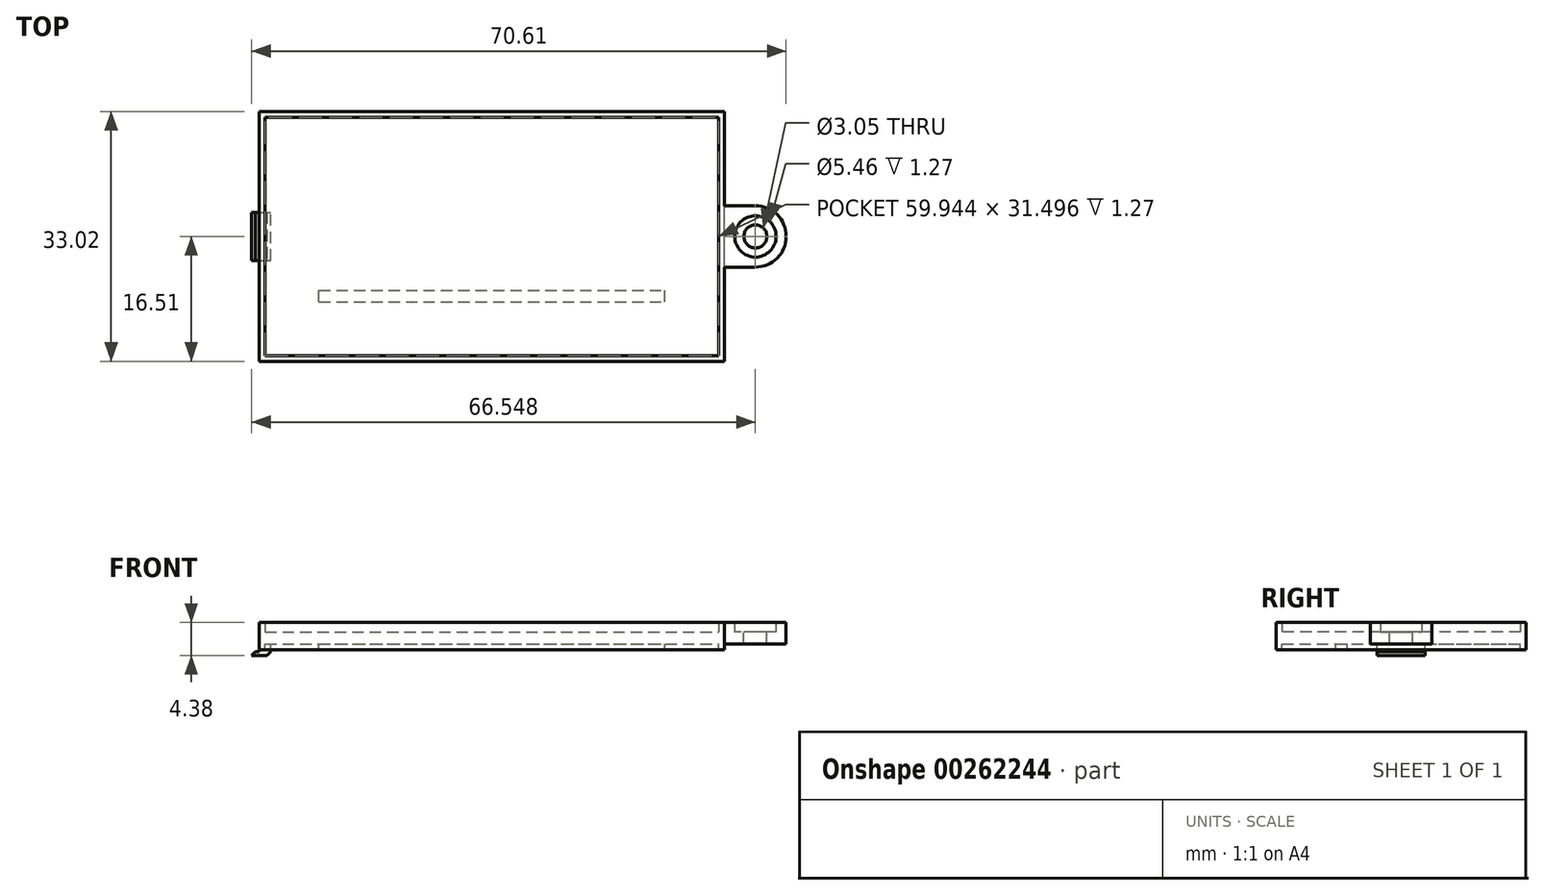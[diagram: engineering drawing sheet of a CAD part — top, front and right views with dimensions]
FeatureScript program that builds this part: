
annotation { "Feature Type Name" : "Feature", "Feature Type Description" : "" }
export const myFeature = defineFeature(function(context is Context, id is Id, definition is map)
    precondition{}
    {
        {
            var Q0;
            Q0=qCreatedBy(makeId("Top.planeOp"),FACE);
            var sketch = newSketch(context, id + "F0", { "sketchPlane" : qUnion([Q0])});
            skLineSegment(sketch, "E0.bottom", {"start": v(30.73, -16.51) * mm, "end": v(-30.73, -16.51) * mm});
            skLineSegment(sketch, "E0.top", {"start": v(30.73, 16.51) * mm, "end": v(-30.73, 16.51) * mm});
            skLineSegment(sketch, "E0.left", {"start": v(30.73, -16.5) * mm, "end": v(30.73, 16.51) * mm});
            skLineSegment(sketch, "E0.right", {"start": v(-30.73, -16.51) * mm, "end": v(-30.73, 16.51) * mm});
            skPoint(sketch, "E0.middle", {"position": v(0, 0) * mm});
            skLineSegment(sketch, "E1", {"start": v(-53.62, 0) * mm, "end": v(52.35, 0) * mm, "construction": true});
            skPoint(sketch, "E1.startSnap0", {"position": v(-30.73, 0) * mm});
            skPoint(sketch, "E1.endSnap0", {"position": v(-30.73, 0) * mm});
            skLineSegment(sketch, "E2", {"start": v(30.73, 4.06) * mm, "end": v(34.8, 4.06) * mm});
            skLineSegment(sketch, "E3", {"start": v(38.86, 0) * mm, "end": v(38.86, 0) * mm});
            skLineSegment(sketch, "E4", {"start": v(34.8, -4.06) * mm, "end": v(30.73, -4.06) * mm});
            skPoint(sketch, "E5.visualSharp", {"position": v(38.86, 4.06) * mm});
            skArc(sketch, "E5.filletArc", {"start": v(38.86, 0) * mm, "mid": v(37.67, 2.87) * mm, "end": v(34.8, 4.06) * mm});
            skPoint(sketch, "E6.visualSharp", {"position": v(38.86, -4.06) * mm});
            skArc(sketch, "E6.filletArc", {"start": v(34.8, -4.06) * mm, "mid": v(37.67, -2.87) * mm, "end": v(38.86, 0) * mm});
            skSolve(sketch);
        }
        {
            var Q0;
            Q0 = qSketchRegion(id + "F0", true);
            extrude(context, id + "F1", {"entities" : qUnion([Q0]), "depth" : 1.59 * mm});
        }
        {
            var Q0;
            Q0=makeQuery(id+"F1.opExtrude","CAP_FACE",FACE,{"disambiguationData":[OSD([sQuery(id+"F0.wireOp",EDGE,"E0.bottom"),sQuery(id+"F0.wireOp",EDGE,"E0.top"),sQuery(id+"F0.wireOp",EDGE,"E0.left"),sQuery(id+"F0.wireOp",EDGE,"E0.right"),sQuery(id+"F0.wireOp",EDGE,"E2"),sQuery(id+"F0.wireOp",EDGE,"E4"),sQuery(id+"F0.wireOp",EDGE,"E5.filletArc"),sQuery(id+"F0.wireOp",EDGE,"E6.filletArc")])],"isStart":false});
            var sketch = newSketch(context, id + "F2", { "sketchPlane" : qUnion([Q0])});
            skCircle(sketch, "E7", {"center": v(34.8, 0) * mm, "radius": 1.52 * mm});
            skSolve(sketch);
        }
        {
            var Q0;
            Q0=makeQuery(id+"F2.imprint","IMPRINT",FACE,{"disambiguationData":[TD([[makeQuery(id+"F2.imprint","IMPRINT",EDGE,{"derivedFrom":sQuery(id+"F2.wireOp",EDGE,"E7")}),1.0]])]});
            extrude(context, id + "F3", {"entities" : qUnion([Q0]), "operationType" : NewBodyOperationType.REMOVE, "endBound" : BoundingType.THROUGH_ALL, "oppositeDirection" : true, "depth" : 25.4 * mm});
        }
        {
            var Q0;
            Q0=makeQuery(id+"F1.opExtrude","CAP_FACE",FACE,{"disambiguationData":[OSD([sQuery(id+"F0.wireOp",EDGE,"E0.bottom"),sQuery(id+"F0.wireOp",EDGE,"E0.top"),sQuery(id+"F0.wireOp",EDGE,"E0.left"),sQuery(id+"F0.wireOp",EDGE,"E0.right"),sQuery(id+"F0.wireOp",EDGE,"E2"),sQuery(id+"F0.wireOp",EDGE,"E4"),sQuery(id+"F0.wireOp",EDGE,"E5.filletArc"),sQuery(id+"F0.wireOp",EDGE,"E6.filletArc")])],"isStart":false});
            var sketch = newSketch(context, id + "F4", { "sketchPlane" : qUnion([Q0])});
            skCircle(sketch, "E8", {"center": v(34.8, 0) * mm, "radius": 2.73 * mm});
            skCircle(sketch, "E9", {"center": v(34.8, 0) * mm, "radius": 4.06 * mm});
            skSolve(sketch);
        }
        {
            var Q0;
            Q0=makeQuery(id+"F4.imprint","IMPRINT",FACE,{"disambiguationData":[TD([[makeQuery(id+"F4.imprint","IMPRINT",EDGE,{"derivedFrom":sQuery(id+"F4.wireOp",EDGE,"E8")}),-1.0]])]});
            extrude(context, id + "F5", {"entities" : qUnion([Q0]), "operationType" : NewBodyOperationType.ADD, "depth" : 1.27 * mm});
        }
        {
            var Q0;
            Q0=makeQuery(id+"F1.opExtrude","CAP_FACE",FACE,{"disambiguationData":[OSD([sQuery(id+"F0.wireOp",EDGE,"E0.bottom"),sQuery(id+"F0.wireOp",EDGE,"E0.top"),sQuery(id+"F0.wireOp",EDGE,"E0.left"),sQuery(id+"F0.wireOp",EDGE,"E0.right"),sQuery(id+"F0.wireOp",EDGE,"E2"),sQuery(id+"F0.wireOp",EDGE,"E4"),sQuery(id+"F0.wireOp",EDGE,"E5.filletArc"),sQuery(id+"F0.wireOp",EDGE,"E6.filletArc")])],"isStart":true});
            var sketch = newSketch(context, id + "F6", { "sketchPlane" : qUnion([Q0])});
            skLineSegment(sketch, "E10.bottom", {"start": v(-30.73, 3.17) * mm, "end": v(-29.21, 3.17) * mm});
            skLineSegment(sketch, "E10.top", {"start": v(-30.73, -3.18) * mm, "end": v(-29.21, -3.18) * mm});
            skLineSegment(sketch, "E10.left", {"start": v(-30.73, 3.17) * mm, "end": v(-30.73, -3.18) * mm});
            skLineSegment(sketch, "E10.right", {"start": v(-29.21, 3.17) * mm, "end": v(-29.21, -3.18) * mm});
            skLineSegment(sketch, "E11", {"start": v(0, 0) * mm, "end": v(-48.3, 0) * mm, "construction": true});
            skSolve(sketch);
        }
        {
            var Q0;
            Q0=makeQuery(id+"F6.imprint","IMPRINT",FACE,{"disambiguationData":[TD([[makeQuery(id+"F6.imprint","IMPRINT",EDGE,{"derivedFrom":sQuery(id+"F6.wireOp",EDGE,"E10.bottom")}),-1.0]])]});
            extrude(context, id + "F7", {"entities" : qUnion([Q0]), "operationType" : NewBodyOperationType.ADD, "depth" : 1.52 * mm});
        }
        {
            var Q0;
            Q0=makeQuery(id+"F7.boolean.opBoolean","MERGE",FACE,{"derivedFrom":[makeQuery(id+"F1.opExtrude","SWEPT_FACE",FACE,{"disambiguationData":[OSD([sQuery(id+"F0.wireOp",EDGE,"E0.right")])]}),makeQuery(id+"F7.opExtrude","SWEPT_FACE",FACE,{"disambiguationData":[OSD([sQuery(id+"F6.wireOp",EDGE,"E10.left")])]})]});
            var sketch = newSketch(context, id + "F8", { "sketchPlane" : qUnion([Q0])});
            skLineSegment(sketch, "E12.bottom", {"start": v(-3.17, -1.52) * mm, "end": v(3.18, -1.52) * mm});
            skLineSegment(sketch, "E12.top", {"start": v(-3.17, -1.02) * mm, "end": v(3.18, -1.02) * mm});
            skLineSegment(sketch, "E12.left", {"start": v(-3.17, -1.52) * mm, "end": v(-3.17, -1.02) * mm});
            skLineSegment(sketch, "E12.right", {"start": v(3.18, -1.52) * mm, "end": v(3.18, -0.23) * mm});
            skSolve(sketch);
        }
        {
            var Q0;
            {var subQ0=sQuery(id+"F8.wireOp",EDGE,"E12.bottom");Q0=makeQuery(id+"F8.imprint","IMPRINT",FACE,{"disambiguationData":[TD([[makeQuery(id+"F8.imprint","IMPRINT",EDGE,{"derivedFrom":subQ0}),-1.0]])]});}
            extrude(context, id + "F9", {"entities" : qUnion([Q0]), "operationType" : NewBodyOperationType.ADD, "depth" : 1.02 * mm});
        }
        {
            var Q0;
            Q0=makeQuery(id+"F9.opExtrude","CAP_EDGE",EDGE,{"disambiguationData":[OSD([sQuery(id+"F8.wireOp",EDGE,"E12.top")])],"isStart":false});
            var Q1;
            Q1=makeQuery(id+"F7.opExtrude","CAP_EDGE",EDGE,{"disambiguationData":[OSD([sQuery(id+"F6.wireOp",EDGE,"E10.right")])],"isStart":false});
            chamfer(context, id + "F10", {"entities" : qUnion([Q0, Q1]), "width" : 0.5 * mm, "tangentPropagation" : true});
        }
        {
            var Q0;
            Q0=makeQuery(id+"F1.opExtrude","CAP_FACE",FACE,{"disambiguationData":[OSD([sQuery(id+"F0.wireOp",EDGE,"E0.bottom"),sQuery(id+"F0.wireOp",EDGE,"E0.top"),sQuery(id+"F0.wireOp",EDGE,"E0.left"),sQuery(id+"F0.wireOp",EDGE,"E0.right"),sQuery(id+"F0.wireOp",EDGE,"E2"),sQuery(id+"F0.wireOp",EDGE,"E4"),sQuery(id+"F0.wireOp",EDGE,"E5.filletArc"),sQuery(id+"F0.wireOp",EDGE,"E6.filletArc")])],"isStart":true});
            var sketch = newSketch(context, id + "F11", { "sketchPlane" : qUnion([Q0])});
            skLineSegment(sketch, "E13.bottom", {"start": v(-29.97, 15.75) * mm, "end": v(29.97, 15.75) * mm});
            skLineSegment(sketch, "E13.top", {"start": v(-29.97, -15.75) * mm, "end": v(29.97, -15.75) * mm});
            skLineSegment(sketch, "E13.left", {"start": v(-29.97, 15.75) * mm, "end": v(-29.97, -15.75) * mm});
            skLineSegment(sketch, "E13.right", {"start": v(29.97, 15.75) * mm, "end": v(29.97, -15.75) * mm});
            skLineSegment(sketch, "E14.bottom", {"start": v(-30.73, 16.51) * mm, "end": v(30.73, 16.51) * mm});
            skLineSegment(sketch, "E14.top", {"start": v(-30.73, -16.51) * mm, "end": v(30.73, -16.51) * mm});
            skLineSegment(sketch, "E14.left", {"start": v(-30.73, 16.51) * mm, "end": v(-30.73, -16.51) * mm});
            skLineSegment(sketch, "E14.right", {"start": v(30.73, 16.51) * mm, "end": v(30.73, -16.51) * mm});
            skSolve(sketch);
        }
        {
            var Q0;
            {var subQ11=sQuery(id+"F11.wireOp",EDGE,"E13.bottom");Q0=makeQuery(id+"F11.imprint","IMPRINT",FACE,{"disambiguationData":[TD([[makeQuery(id+"F11.imprint","IMPRINT",EDGE,{"derivedFrom":subQ11}),1.0]])]});}
            extrude(context, id + "F12", {"entities" : qUnion([Q0]), "operationType" : NewBodyOperationType.ADD, "depth" : 0.76 * mm});
        }
        {
            var Q0;
            {var subQ0=sQuery(id+"F0.wireOp",EDGE,"E0.left");var subQ1=sQuery(id+"F0.wireOp",EDGE,"E0.top");var subQ2=sQuery(id+"F0.wireOp",EDGE,"E2");var subQ3=sQuery(id+"F0.wireOp",EDGE,"E0.bottom");var subQ4=sQuery(id+"F0.wireOp",EDGE,"E4");var subQ5=sQuery(id+"F0.wireOp",EDGE,"E0.right");var subQ6=sQuery(id+"F0.wireOp",EDGE,"E6.filletArc");var subQ7=sQuery(id+"F0.wireOp",EDGE,"E5.filletArc");Q0=makeQuery(id+"F5.boolean.opBoolean","SPLIT",FACE,{"disambiguationData":[TD([makeQuery(id+"F1.opExtrude","SWEPT_FACE",FACE,{"disambiguationData":[OSD([subQ3])]})])],"derivedFrom":makeQuery(id+"F1.opExtrude","CAP_FACE",FACE,{"disambiguationData":[OSD([subQ3,subQ1,subQ0,subQ5,subQ2,subQ4,subQ7,subQ6])],"isStart":false})});}
            var sketch = newSketch(context, id + "F13", { "sketchPlane" : qUnion([Q0])});
            skLineSegment(sketch, "E15.bottom", {"start": v(-30.73, 16.51) * mm, "end": v(30.73, 16.51) * mm});
            skLineSegment(sketch, "E15.top", {"start": v(-30.73, -16.51) * mm, "end": v(30.73, -16.51) * mm});
            skLineSegment(sketch, "E15.left", {"start": v(-30.73, 16.51) * mm, "end": v(-30.73, -16.51) * mm});
            skLineSegment(sketch, "E15.right", {"start": v(30.73, 16.51) * mm, "end": v(30.73, -16.51) * mm});
            skLineSegment(sketch, "E16.bottom", {"start": v(-29.97, 15.75) * mm, "end": v(29.97, 15.75) * mm});
            skLineSegment(sketch, "E16.top", {"start": v(-29.97, -15.75) * mm, "end": v(29.97, -15.75) * mm});
            skLineSegment(sketch, "E16.left", {"start": v(-29.97, 15.75) * mm, "end": v(-29.97, -15.75) * mm});
            skLineSegment(sketch, "E16.right", {"start": v(29.97, 15.75) * mm, "end": v(29.97, -15.75) * mm});
            skSolve(sketch);
        }
        {
            var Q0;
            {var subQ1=makeQuery(id+"F1.opExtrude","CAP_EDGE",EDGE,{"disambiguationData":[OSD([sQuery(id+"F0.wireOp",EDGE,"E4")])],"isStart":false});Q0=makeQuery(id+"F13.imprint","IMPRINT",FACE,{"disambiguationData":[TD([[makeQuery(id+"F13.imprint","IMPRINT",EDGE,{"derivedFrom":subQ1}),-1.0]])]});}
            var Q1;
            {var subQ1=makeQuery(id+"F1.opExtrude","CAP_EDGE",EDGE,{"disambiguationData":[OSD([sQuery(id+"F0.wireOp",EDGE,"E2")])],"isStart":false});Q1=makeQuery(id+"F13.imprint","IMPRINT",FACE,{"disambiguationData":[TD([[makeQuery(id+"F13.imprint","IMPRINT",EDGE,{"derivedFrom":subQ1}),-1.0]])]});}
            var Q2;
            {var subQ0=sQuery(id+"F13.wireOp",EDGE,"E15.bottom");Q2=makeQuery(id+"F13.imprint","IMPRINT",FACE,{"disambiguationData":[TD([[makeQuery(id+"F13.imprint","IMPRINT",EDGE,{"derivedFrom":subQ0}),1.0]])]});}
            var Q3;
            Q3=makeQuery(id+"F5.opExtrude","CAP_FACE",FACE,{"disambiguationData":[OSD([sQuery(id+"F4.wireOp",EDGE,"E8"),sQuery(id+"F4.wireOp",EDGE,"E9")])],"isStart":false});
            extrude(context, id + "F14", {"entities" : qUnion([Q0, Q1, Q2]), "operationType" : NewBodyOperationType.ADD, "endBound" : BoundingType.UP_TO_SURFACE, "endBoundEntityFace" : qUnion([Q3]), "depth" : 25.4 * mm});
        }
        {
            var Q0;
            {var subQ1=sQuery(id+"F6.wireOp",EDGE,"E10.bottom");Q0=makeQuery(id+"F12.boolean.opBoolean","SPLIT",FACE,{"disambiguationData":[TD([makeQuery(id+"F7.opExtrude","SWEPT_FACE",FACE,{"disambiguationData":[OSD([subQ1])]})])],"derivedFrom":makeQuery(id+"F1.opExtrude","CAP_FACE",FACE,{"disambiguationData":[OSD([sQuery(id+"F0.wireOp",EDGE,"E0.bottom"),sQuery(id+"F0.wireOp",EDGE,"E0.top"),sQuery(id+"F0.wireOp",EDGE,"E0.left"),sQuery(id+"F0.wireOp",EDGE,"E0.right"),sQuery(id+"F0.wireOp",EDGE,"E2"),sQuery(id+"F0.wireOp",EDGE,"E4"),sQuery(id+"F0.wireOp",EDGE,"E5.filletArc"),sQuery(id+"F0.wireOp",EDGE,"E6.filletArc")])],"isStart":true})});}
            var sketch = newSketch(context, id + "F15", { "sketchPlane" : qUnion([Q0])});
            skLineSegment(sketch, "E17.bottom", {"start": v(-22.86, 8.64) * mm, "end": v(22.86, 8.64) * mm});
            skLineSegment(sketch, "E17.top", {"start": v(-22.86, 7.11) * mm, "end": v(22.86, 7.11) * mm});
            skLineSegment(sketch, "E17.left", {"start": v(-22.86, 8.64) * mm, "end": v(-22.86, 7.11) * mm});
            skLineSegment(sketch, "E17.right", {"start": v(22.86, 8.64) * mm, "end": v(22.86, 7.11) * mm});
            skSolve(sketch);
        }
        {
            var Q0;
            Q0=makeQuery(id+"F15.imprint","IMPRINT",FACE,{"disambiguationData":[TD([[makeQuery(id+"F15.imprint","IMPRINT",EDGE,{"derivedFrom":sQuery(id+"F15.wireOp",EDGE,"E17.bottom")}),-1.0]])]});
            extrude(context, id + "F16", {"entities" : qUnion([Q0]), "operationType" : NewBodyOperationType.ADD, "depth" : 0.76 * mm});
        }
    });
